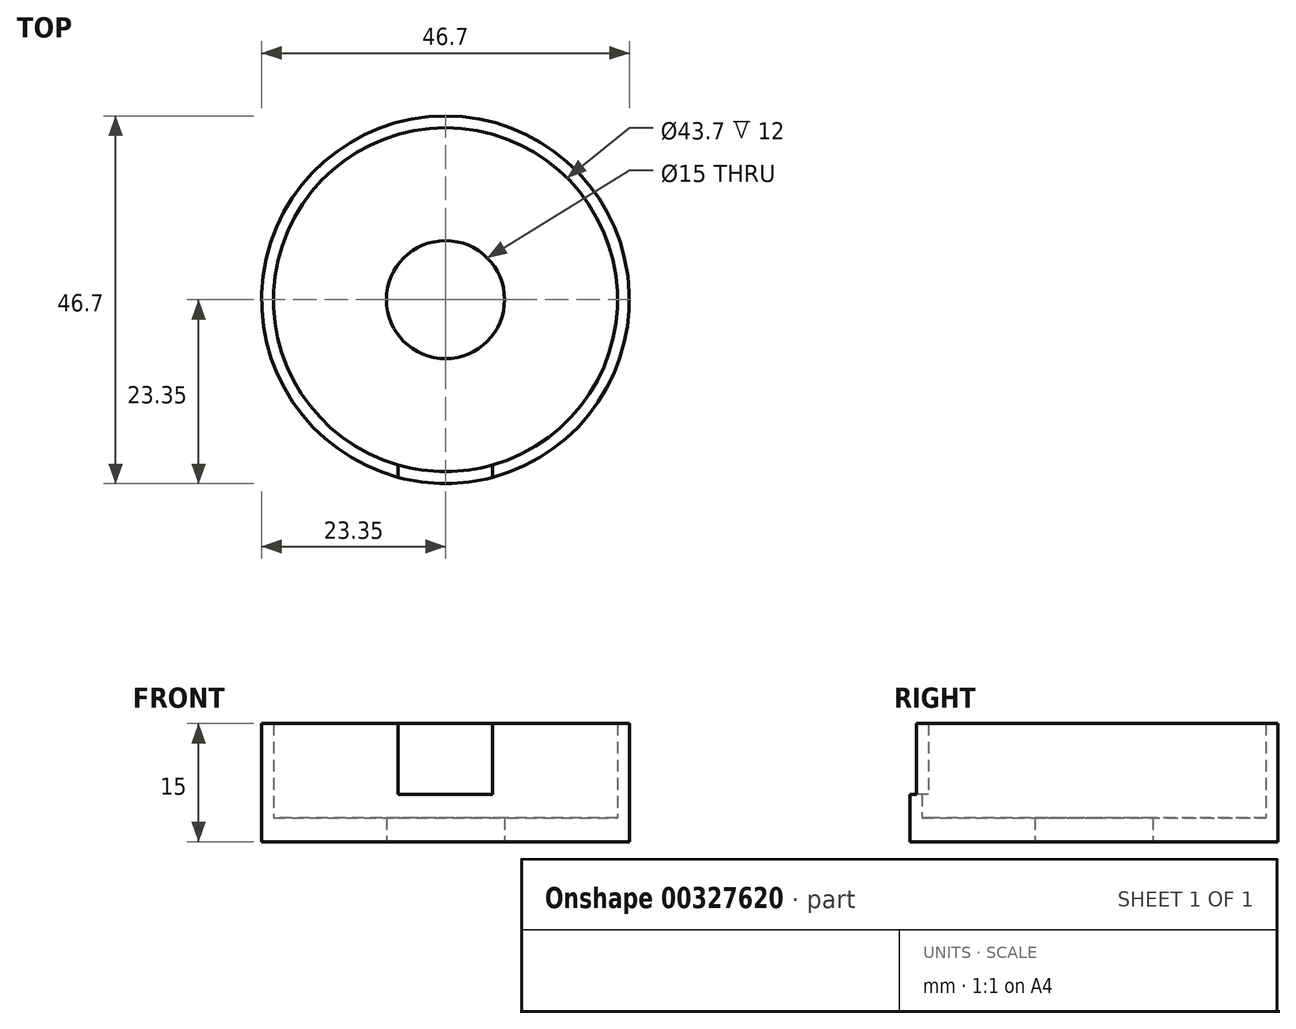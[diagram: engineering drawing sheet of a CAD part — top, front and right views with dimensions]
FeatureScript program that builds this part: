
annotation { "Feature Type Name" : "Feature", "Feature Type Description" : "" }
export const myFeature = defineFeature(function(context is Context, id is Id, definition is map)
    precondition{}
    {
        {
            var Q0;
            Q0=qCreatedBy(makeId("Top.planeOp"),FACE);
            var sketch = newSketch(context, id + "F0", { "sketchPlane" : qUnion([Q0])});
            skCircle(sketch, "E0", {"center": v(0, 0) * mm, "radius": 21.85 * mm});
            skCircle(sketch, "E1", {"center": v(0, 0) * mm, "radius": 23.35 * mm});
            skSolve(sketch);
        }
        {
            var Q0;
            Q0 = qSketchRegion(id + "F0", true);
            extrude(context, id + "F1", {"entities" : qUnion([Q0]), "depth" : 15 * mm});
        }
        {
            var Q0;
            Q0=makeQuery(id+"F0.imprint","IMPRINT",FACE,{"disambiguationData":[TD([[makeQuery(id+"F0.imprint","IMPRINT",EDGE,{"derivedFrom":sQuery(id+"F0.wireOp",EDGE,"E0")}),1.0]])]});
            extrude(context, id + "F2", {"entities" : qUnion([Q0]), "operationType" : NewBodyOperationType.ADD, "depth" : 3 * mm});
        }
        {
            var Q0;
            Q0=qCreatedBy(makeId("Top.planeOp"),FACE);
            var sketch = newSketch(context, id + "F3", { "sketchPlane" : qUnion([Q0])});
            skCircle(sketch, "E2", {"center": v(0, 0) * mm, "radius": 7.5 * mm});
            skSolve(sketch);
        }
        {
            var Q0;
            Q0 = qSketchRegion(id + "F3", true);
            extrude(context, id + "F4", {"entities" : qUnion([Q0]), "operationType" : NewBodyOperationType.REMOVE, "depth" : 25.4 * mm});
        }
        {
            var Q0;
            Q0=makeQuery(id+"F1.opExtrude","CAP_FACE",FACE,{"disambiguationData":[OSD([sQuery(id+"F0.wireOp",EDGE,"E0"),sQuery(id+"F0.wireOp",EDGE,"E1")])],"isStart":false});
            cPlane(context, id + "F5", {"entities" : qUnion([Q0]), "cplaneType" : CPlaneType.OFFSET, "offset" : 0 * mm, "width" : 152.4 * mm, "height" : 152.4 * mm});
        }
        {
            var Q0;
            Q0=qCreatedBy(id+"F5.planeOp",FACE);
            var sketch = newSketch(context, id + "F6", { "sketchPlane" : qUnion([Q0])});
            skLineSegment(sketch, "E3.bottom", {"start": v(-6, -18.8) * mm, "end": v(6, -18.8) * mm});
            skLineSegment(sketch, "E3.top", {"start": v(-6, -25.6) * mm, "end": v(6, -25.6) * mm});
            skLineSegment(sketch, "E3.left", {"start": v(-6, -18.8) * mm, "end": v(-6, -25.6) * mm});
            skLineSegment(sketch, "E3.right", {"start": v(6, -18.8) * mm, "end": v(6, -25.6) * mm});
            skSolve(sketch);
        }
        {
            var Q0;
            Q0 = qSketchRegion(id + "F6", true);
            extrude(context, id + "F7", {"entities" : qUnion([Q0]), "operationType" : NewBodyOperationType.REMOVE, "oppositeDirection" : true, "depth" : 9 * mm, "offsetDistance" : 25.4 * mm});
        }
    });
